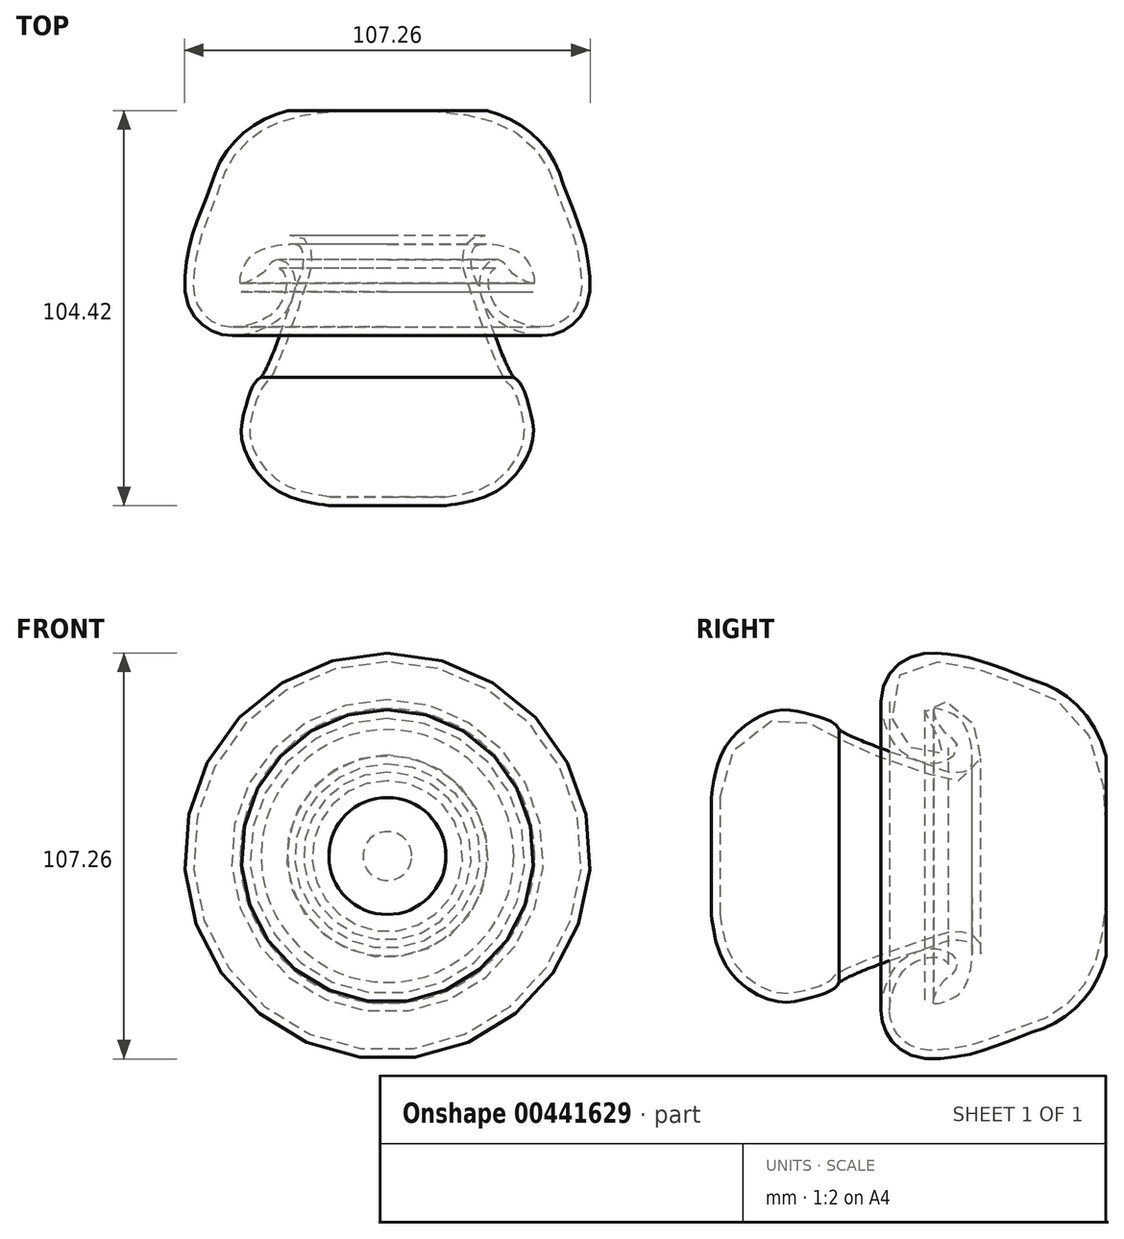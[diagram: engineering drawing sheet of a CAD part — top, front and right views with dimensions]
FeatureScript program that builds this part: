
annotation { "Feature Type Name" : "Feature", "Feature Type Description" : "" }
export const myFeature = defineFeature(function(context is Context, id is Id, definition is map)
    precondition{}
    {
        {
            var Q0;
            Q0=qCreatedBy(makeId("Top.planeOp"),FACE);
            var sketch = newSketch(context, id + "F0", { "sketchPlane" : qUnion([Q0])});
            skLineSegment(sketch, "E0", {"start": v(0, -47.93) * mm, "end": v(15.3, -47.93) * mm});
            skFitSpline(sketch, "E1", {"points": [v(15.3, -47.93) * mm, v(28.57, -43.88) * mm, v(35.95, -33.55) * mm, v(35.58, -25.8) * mm, v(33, -18.8) * mm, v(31.9, -18.07) * mm, v(26, -5.16) * mm, v(21.2, 8.85) * mm, v(20.1, 12.17) * mm, v(21.2, 19.54) * mm, v(27.84, 21.02) * mm, v(34.1, 19.54) * mm, v(38.9, 15.85) * mm, v(41.11, 7.74) * mm, v(38.53, 6.27) * mm, v(34.1, 7.74) * mm, v(30.42, 10.7) * mm, v(28.57, 12.54) * mm, v(26.73, 9.22) * mm, v(28.2, 3.32) * mm, v(31.16, 0) * mm, v(42.22, -2.95) * mm, v(50.33, 2.95) * mm, v(51.07, 12.17) * mm, v(49.22, 21.02) * mm, v(44.8, 32.82) * mm, v(41.85, 40.19) * mm, v(33, 49.04) * mm, v(18.25, 53.46) * mm, v(6.45, 54.2) * mm], "startDerivative": vector(307.77, 45.73) * mm, "endDerivative": vector(-265.75, 6.76) * mm});
            skLineSegment(sketch, "E2", {"start": v(6.45, 54.2) * mm, "end": v(0, 54.2) * mm});
            skLineSegment(sketch, "E3", {"start": v(0, 54.2) * mm, "end": v(0, 74.85) * mm});
            skLineSegment(sketch, "E4", {"start": v(0, 74.85) * mm, "end": v(0, -70.42) * mm});
            skSolve(sketch);
        }
        {
            var Q0;
            {var subQ0=sQuery(id+"F0.wireOp",EDGE,"E0");Q0=makeQuery(id+"F0.imprint","IMPRINT",FACE,{"disambiguationData":[TD([[makeQuery(id+"F0.imprint","IMPRINT",EDGE,{"derivedFrom":subQ0}),1.0]])]});}
            var Q1;
            Q1=sQuery(id+"F0.wireOp",EDGE,"E4");
            revolve(context, id + "F1", {"entities" : qUnion([Q0]), "axis" : qUnion([Q1]), "revolveType" : RevolveType.FULL});
        }
        {
            var Q0;
            Q0=makeQuery(id+"F1.opRevolve","SWEPT_FACE",FACE,{"disambiguationData":[OSD([sQuery(id+"F0.wireOp",EDGE,"E2")])]});
            shell(context, id + "F2", {"entities" : qUnion([Q0]), "thickness" : 2.3 * mm, "oppositeDirection" : true});
        }
    });
